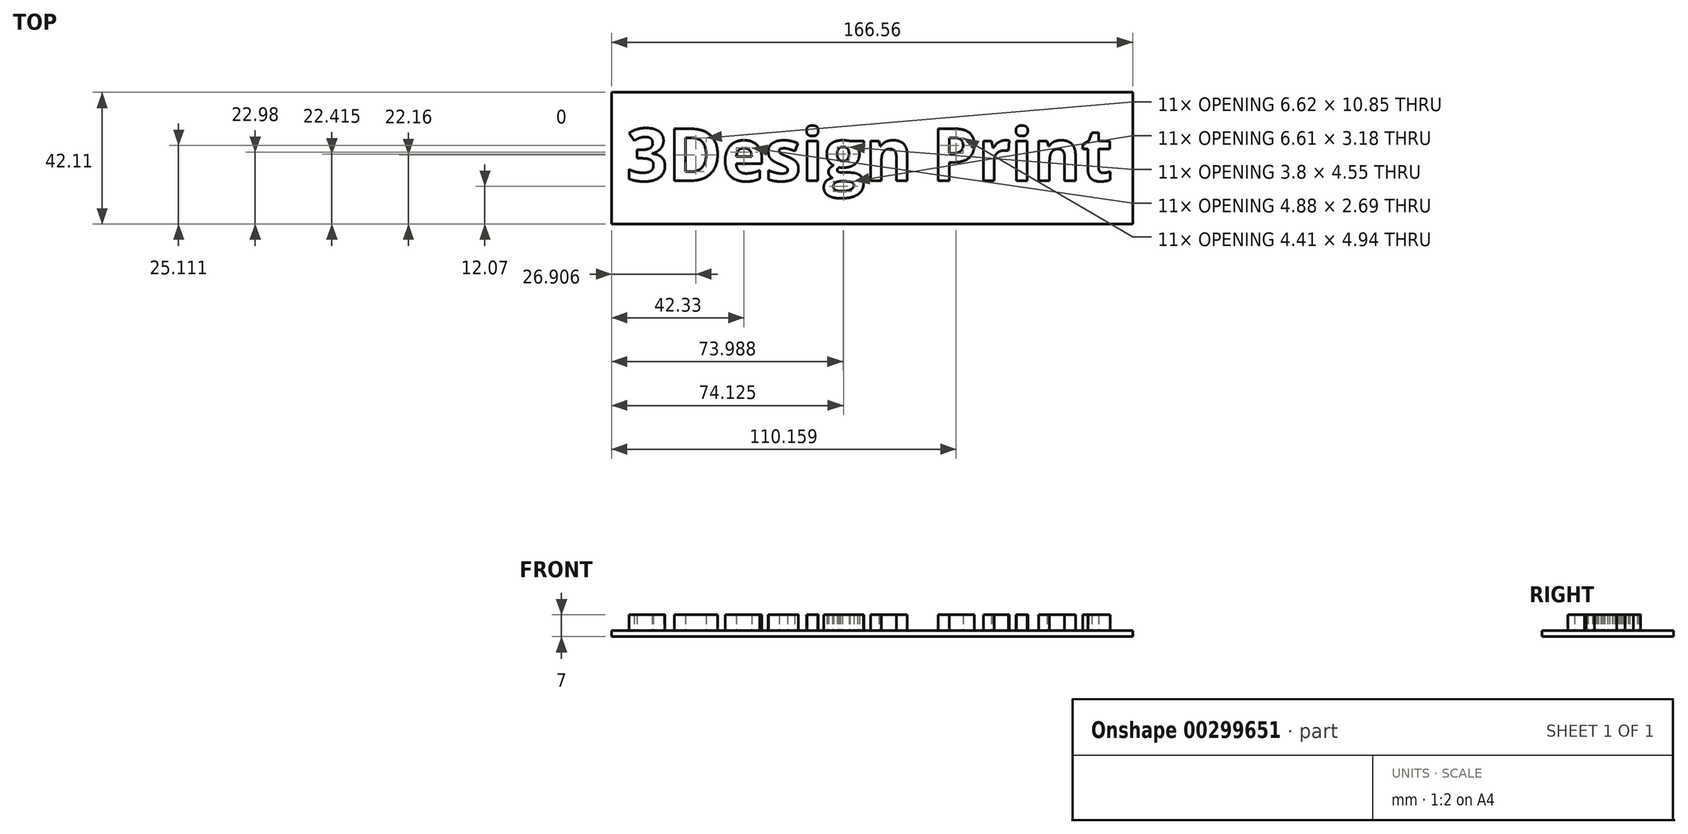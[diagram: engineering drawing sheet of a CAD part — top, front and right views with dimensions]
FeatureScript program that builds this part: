
annotation { "Feature Type Name" : "Feature", "Feature Type Description" : "" }
export const myFeature = defineFeature(function(context is Context, id is Id, definition is map)
    precondition{}
    {
        {
            var Q0;
            Q0=qCreatedBy(makeId("Top.planeOp"),FACE);
            var sketch = newSketch(context, id + "F0", { "sketchPlane" : qUnion([Q0])});
            skText(sketch, "E0", { "text": "3Design Print", "fontName": "OpenSans-Bold.ttf"});
            const initialGuessF0  = {"E0": [-0.15627, 0, 1, 0, 0.0168]};
            skSetInitialGuess(sketch, initialGuessF0);
            skSolve(sketch);
        }
        {
            var Q0;
            Q0=qCreatedBy(makeId("Top.planeOp"),FACE);
            var sketch = newSketch(context, id + "F1", { "sketchPlane" : qUnion([Q0])});
            skLineSegment(sketch, "E1.bottom", {"start": v(-160.92, 28.29) * mm, "end": v(5.64, 28.29) * mm});
            skLineSegment(sketch, "E1.top", {"start": v(-160.92, -13.82) * mm, "end": v(5.64, -13.82) * mm});
            skLineSegment(sketch, "E1.left", {"start": v(-160.92, 28.29) * mm, "end": v(-160.92, -13.82) * mm});
            skLineSegment(sketch, "E1.right", {"start": v(5.64, 28.29) * mm, "end": v(5.64, -13.82) * mm});
            skSolve(sketch);
        }
        {
            var Q0;
            Q0 = qSketchRegion(id + "F0", true);
            extrude(context, id + "F2", {"entities" : qUnion([Q0]), "depth" : 5 * mm});
        }
        {
            var Q0;
            Q0 = qSketchRegion(id + "F1", true);
            extrude(context, id + "F3", {"entities" : qUnion([Q0]), "depth" : -2 * mm});
        }
    });
